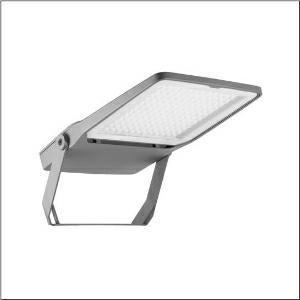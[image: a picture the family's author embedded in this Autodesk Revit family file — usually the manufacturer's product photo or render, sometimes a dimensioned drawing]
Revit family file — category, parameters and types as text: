
# Revit family: floodlight_fl_20_midi___rs17_5xa7682e2b1ac_5cc3
name_source: partatom
category: Lighting Fixtures
units: mm (PartAtom-declared; Revit-internal decimal feet)

## family parameters
Cut with Voids When Loaded = No
Host = Face
Light Source = No
Part Type = Normal
Room Calculation Point = No
Round Connector Dimension = Use Diameter
Shared = No

## types (1)
- --- (1 x LED 4000K / CRI = 70 (unbekannt), 29150 lm, 4000K)
    Apparent Load = 208 VA
    CIE Flux Codes = 79 92 99 100 100
    Color Rendering = 70
    Color Temperature = 4000K
    Default Elevation = 1800 mm
    Description = Floodlight FL 20 midi, floodlight, primary light control with lens, of plastic, primary optical cover: protective disc, of toughened safety glass, transparent, light distribution: RS17, light emission: direct distribution, primary light characteristic: rotationally symmetric, installation type: surface-mounted, LED High Power LED, rated luminous flux: 29.150 lm, light colour: 740, colour temperature: 4000K, control gear: ECG Plus, control: flexible luminous flux parameterisation, time-dependent luminous flux control, digital communication interface, power reduction, overheat protection, electronic power reduction, with terminal, 5-pole, max. 2.5mm², mains connection: 220..240V, AC, 50/60Hz, rated input power: 208W, LED unit, of diecast aluminium, powder-coated, Siteco® metallic grey (DB 702S), length: 654 mm, width: 450 mm, height: 76mm, housing frame, of diecast aluminium, powder-coated, Siteco® metallic grey (DB 702S), mounting bracket, of steel, powder-coated, Siteco® metallic grey (DB 702S), DALIprotection rating (complete): IP66, insulation class (complete): insulation class II (safety insulation), certification: CE, ENEC, VDE, protection symbol: D, permissible ambient temperature for indoor applications: -40..+40°C, permissible ambient temperature for outdoor applications: -40..+50°C, standard: DIN EN 12944, packaging unit: 1 piece

Light Distribution: RS17
    Height = 76 mm
    Lamp = 1 x LED 4000K / CRI >= 70 (unbekannt)
    Lamp Light Flux = 29150 lm
    Lamp count = 1
    Length = 672 mm
    Luminous efficacy = 140 lm/W
    Manufacturer = Siteco
    ModVariant = No
    Model = 5XA7682E2B1AC
    Number of Poles = 1
    OnlyDefault = Yes
    Power Factor = 1
    Product Name = Floodlight FL 20 midi | RS17
    Product group = floodlight | pylon top
    ProductGroupID = 6101
    Protection Class = Protection class II
    Protection Degree = IP 66
    RLX_Detail_Level = 1
    RlxData = <blob elided: 92265 chars, md5=94154742>
    Socket = socket
    Standby Power = 0 W
    System Light Flux = 29150 lm
    System Power = 208 W
    Type Comments = factory setting: luminous flux: 100 % | dim-lin: 254 | 484 mA
    Type Image = l_1005943.jpg
    URL = http://relux.com
    VarID = @adj_141813
    Voltage = 0 V
    Weight = 0.00 kg
    Width = 450 mm

## geometry (parser evidence)
native form markers: Blend x4, Sweep x11
no freeform markers — native parametric forms only
